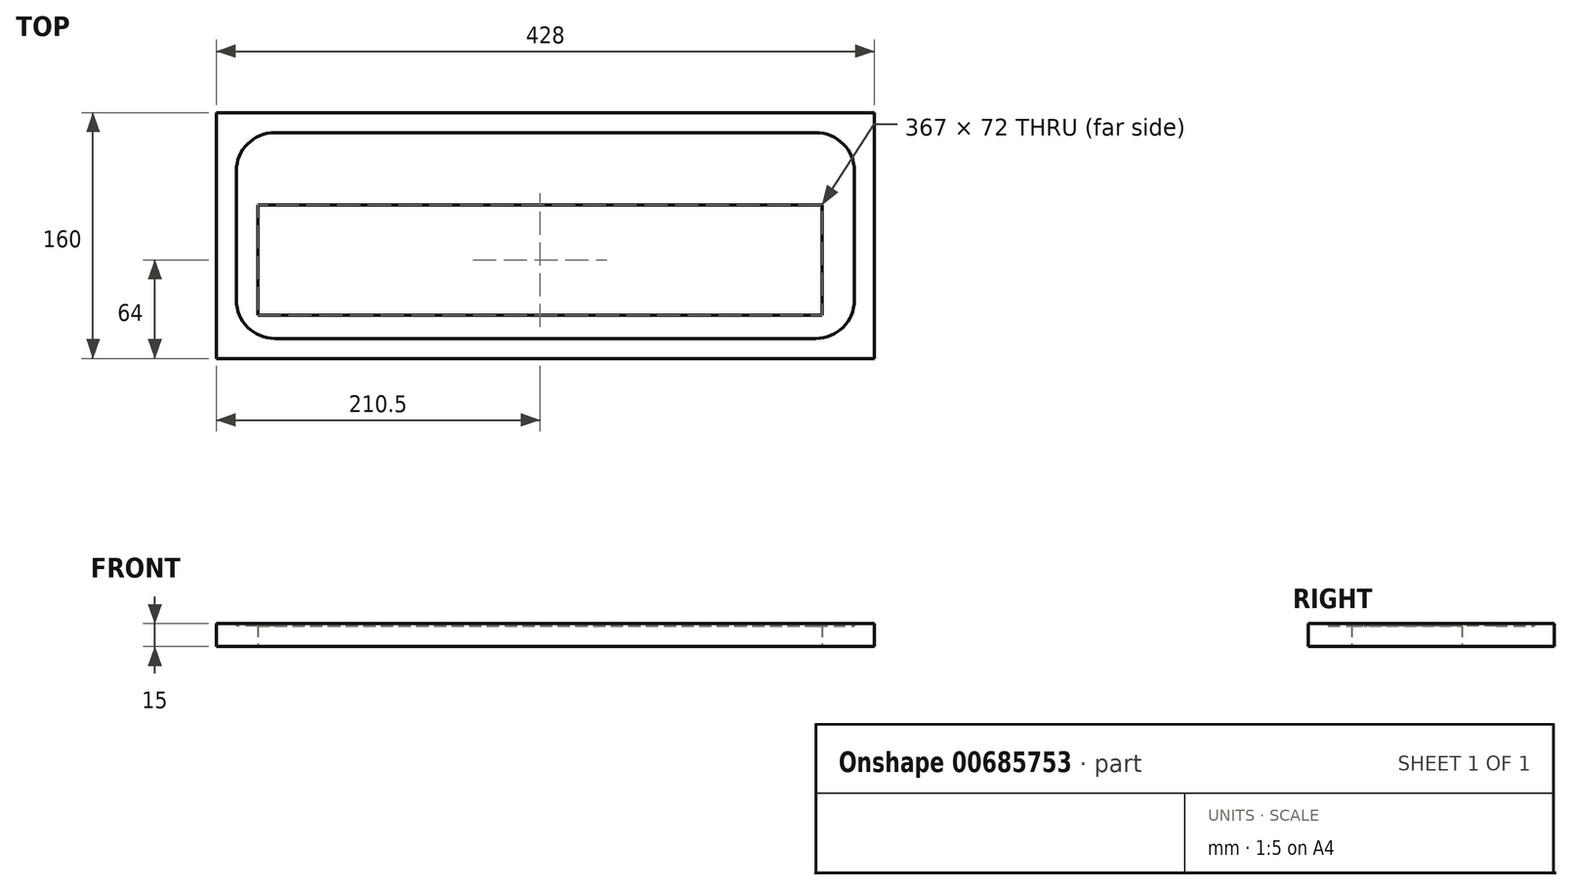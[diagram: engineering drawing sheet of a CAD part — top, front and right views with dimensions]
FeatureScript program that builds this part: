
annotation { "Feature Type Name" : "Feature", "Feature Type Description" : "" }
export const myFeature = defineFeature(function(context is Context, id is Id, definition is map)
    precondition{}
    {
        {
            var Q0;
            Q0=qCreatedBy(makeId("Top.planeOp"),FACE);
            var sketch = newSketch(context, id + "F0", { "sketchPlane" : qUnion([Q0])});
            skLineSegment(sketch, "E0.bottom", {"start": v(0, 0) * mm, "end": v(428, 0) * mm});
            skLineSegment(sketch, "E0.top", {"start": v(0, -160) * mm, "end": v(428, -160) * mm});
            skLineSegment(sketch, "E0.left", {"start": v(0, 0) * mm, "end": v(0, -160) * mm});
            skLineSegment(sketch, "E0.right", {"start": v(428, 0) * mm, "end": v(428, -160) * mm});
            skLineSegment(sketch, "E1.0", {"start": v(13, -13) * mm, "end": v(415, -13) * mm});
            skLineSegment(sketch, "E1.1", {"start": v(13, -13) * mm, "end": v(13, -147) * mm});
            skLineSegment(sketch, "E1.2", {"start": v(13, -147) * mm, "end": v(415, -147) * mm});
            skLineSegment(sketch, "E1.3", {"start": v(415, -13) * mm, "end": v(415, -147) * mm});
            skLineSegment(sketch, "E2.bottom", {"start": v(214, -132) * mm, "end": v(394, -132) * mm});
            skLineSegment(sketch, "E2.top", {"start": v(214, -60) * mm, "end": v(394, -60) * mm});
            skLineSegment(sketch, "E2.right", {"start": v(394, -132) * mm, "end": v(394, -60) * mm});
            skLineSegment(sketch, "E3.bottom", {"start": v(214, -132) * mm, "end": v(27, -132) * mm});
            skLineSegment(sketch, "E3.top", {"start": v(214, -60) * mm, "end": v(27, -60) * mm});
            skLineSegment(sketch, "E3.right", {"start": v(27, -132) * mm, "end": v(27, -60) * mm});
            skSolve(sketch);
        }
        {
            var Q0;
            Q0=makeQuery(id+"F0.imprint","IMPRINT",FACE,{"disambiguationData":[TD([[makeQuery(id+"F0.imprint","IMPRINT",EDGE,{"derivedFrom":sQuery(id+"F0.wireOp",EDGE,"E0.bottom")}),-1.0]])]});
            extrude(context, id + "F1", {"entities" : qUnion([Q0]), "depth" : 15 * mm, "offsetDistance" : 25 * mm});
        }
        {
            var Q0;
            {var subQ5=sQuery(id+"F0.wireOp",EDGE,"E1.0");Q0=makeQuery(id+"F0.imprint","IMPRINT",FACE,{"disambiguationData":[TD([[makeQuery(id+"F0.imprint","IMPRINT",EDGE,{"derivedFrom":subQ5}),-1.0]])]});}
            extrude(context, id + "F2", {"entities" : qUnion([Q0]), "operationType" : NewBodyOperationType.ADD, "depth" : 13.5 * mm, "offsetDistance" : 25 * mm});
        }
        {
            var Q0;
            Q0=makeQuery(id+"F1.opExtrude","SWEPT_EDGE",EDGE,{"disambiguationData":[OSD([sQuery(id+"F0.wireOp",EDGE,"E1.0"),sQuery(id+"F0.wireOp",EDGE,"E1.1")])]});
            var Q1;
            Q1=makeQuery(id+"F1.opExtrude","SWEPT_EDGE",EDGE,{"disambiguationData":[OSD([sQuery(id+"F0.wireOp",EDGE,"E1.1"),sQuery(id+"F0.wireOp",EDGE,"E1.2")])]});
            var Q2;
            Q2=makeQuery(id+"F1.opExtrude","SWEPT_EDGE",EDGE,{"disambiguationData":[OSD([sQuery(id+"F0.wireOp",EDGE,"E1.0"),sQuery(id+"F0.wireOp",EDGE,"E1.3")])]});
            var Q3;
            Q3=makeQuery(id+"F1.opExtrude","SWEPT_EDGE",EDGE,{"disambiguationData":[OSD([sQuery(id+"F0.wireOp",EDGE,"E1.2"),sQuery(id+"F0.wireOp",EDGE,"E1.3")])]});
            fillet(context, id + "F3", {"entities" : qUnion([Q0, Q1, Q2, Q3]), "radius" : 25 * mm, "tangentPropagation" : true, "allowEdgeOverflow" : false});
        }
    });
